# Revit family: Specialty Equipment_Coat Hook_Metlam_ML202-CBNB9c26f0b3-dce3-426c-8e5b-fdd9570f7bba
name_source: partatom
category: Specialty Equipment
revit_build: Autodesk Revit 2014 (Build: 20130308_1515(x64)
units: mm (PartAtom-declared; Revit-internal decimal feet)

## types (1)
- 18w x 73h x 93d
    Assembly Code = C1030200
    Description = Coat Hook
    Manufacturer = Metlam
    Manufacturer_Overall Depth = 93 mm  [stored 0.305118 ft]
    Manufacturer_Overall Height = 73 mm  [stored 0.239501 ft]
    Manufacturer_Overall Width = 18 mm  [stored 0.0590551 ft]
    Manufacturer_Spec Code = ML202-CBNP
    Manufacturer_URL__Product Specific = http://www.metlam.com.au
    Material = z_Metlam_Metal_Brush-Nickel-Satin
    Material Bumper = z_Metlam_Rubber
    Model = ML202-CBNP
    ModifiedIssue_ANZRS = 20150127 $
    Type Comments = ML202-CBNP
    URL = www.metlam.com.au

note: [stored X ft] marks values corroborated as IEEE doubles in the binary element streams (Revit-internal decimal feet)

## geometry (parser evidence)
native form markers: Sweep x2
no freeform markers — native parametric forms only
